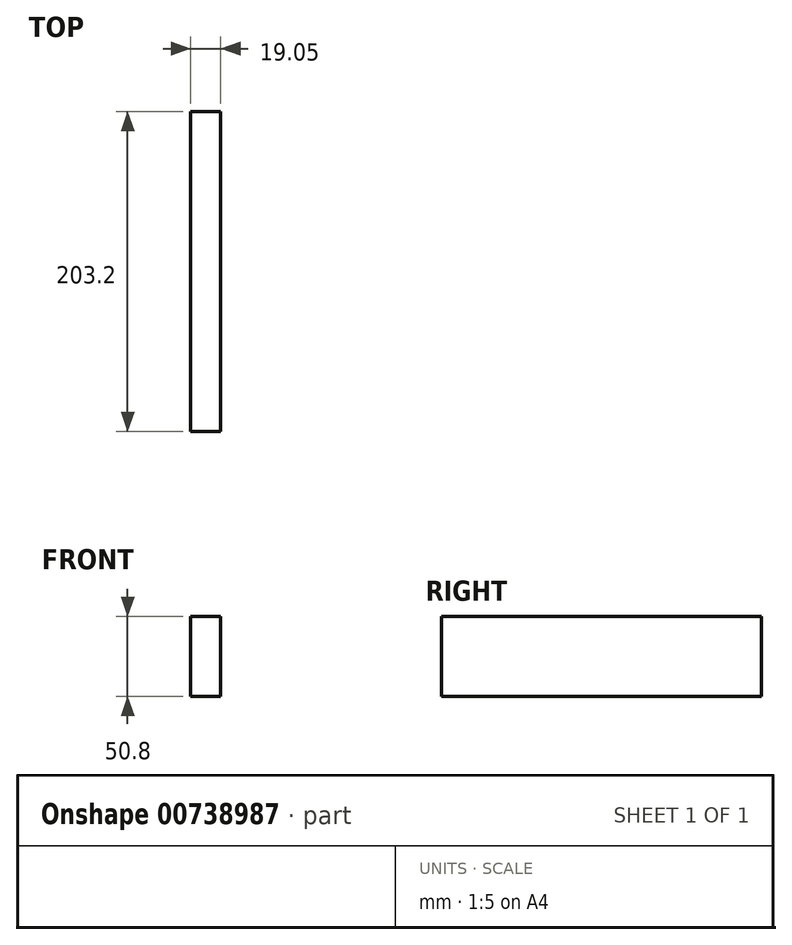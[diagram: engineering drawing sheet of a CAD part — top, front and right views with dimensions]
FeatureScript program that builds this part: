
annotation { "Feature Type Name" : "Feature", "Feature Type Description" : "" }
export const myFeature = defineFeature(function(context is Context, id is Id, definition is map)
    precondition{}
    {
        {
            var Q0;
            Q0=qCreatedBy(makeId("Right.planeOp"),FACE);
            var sketch = newSketch(context, id + "F0", { "sketchPlane" : qUnion([Q0])});
            skLineSegment(sketch, "E0.bottom", {"start": v(-121.98, 0) * mm, "end": v(81.22, 0) * mm});
            skLineSegment(sketch, "E0.top", {"start": v(-121.98, -50.8) * mm, "end": v(81.22, -50.8) * mm});
            skLineSegment(sketch, "E0.left", {"start": v(-121.98, 0) * mm, "end": v(-121.98, -50.8) * mm});
            skLineSegment(sketch, "E0.right", {"start": v(81.22, 0) * mm, "end": v(81.22, -50.8) * mm});
            skSolve(sketch);
        }
        {
            var Q0;
            Q0=qSketchRegion(id+"F0",true);
            extrude(context, id + "F1", {"entities" : qUnion([Q0]), "depth" : 19.05 * mm, "offsetDistance" : 25.4 * mm});
        }
    });
